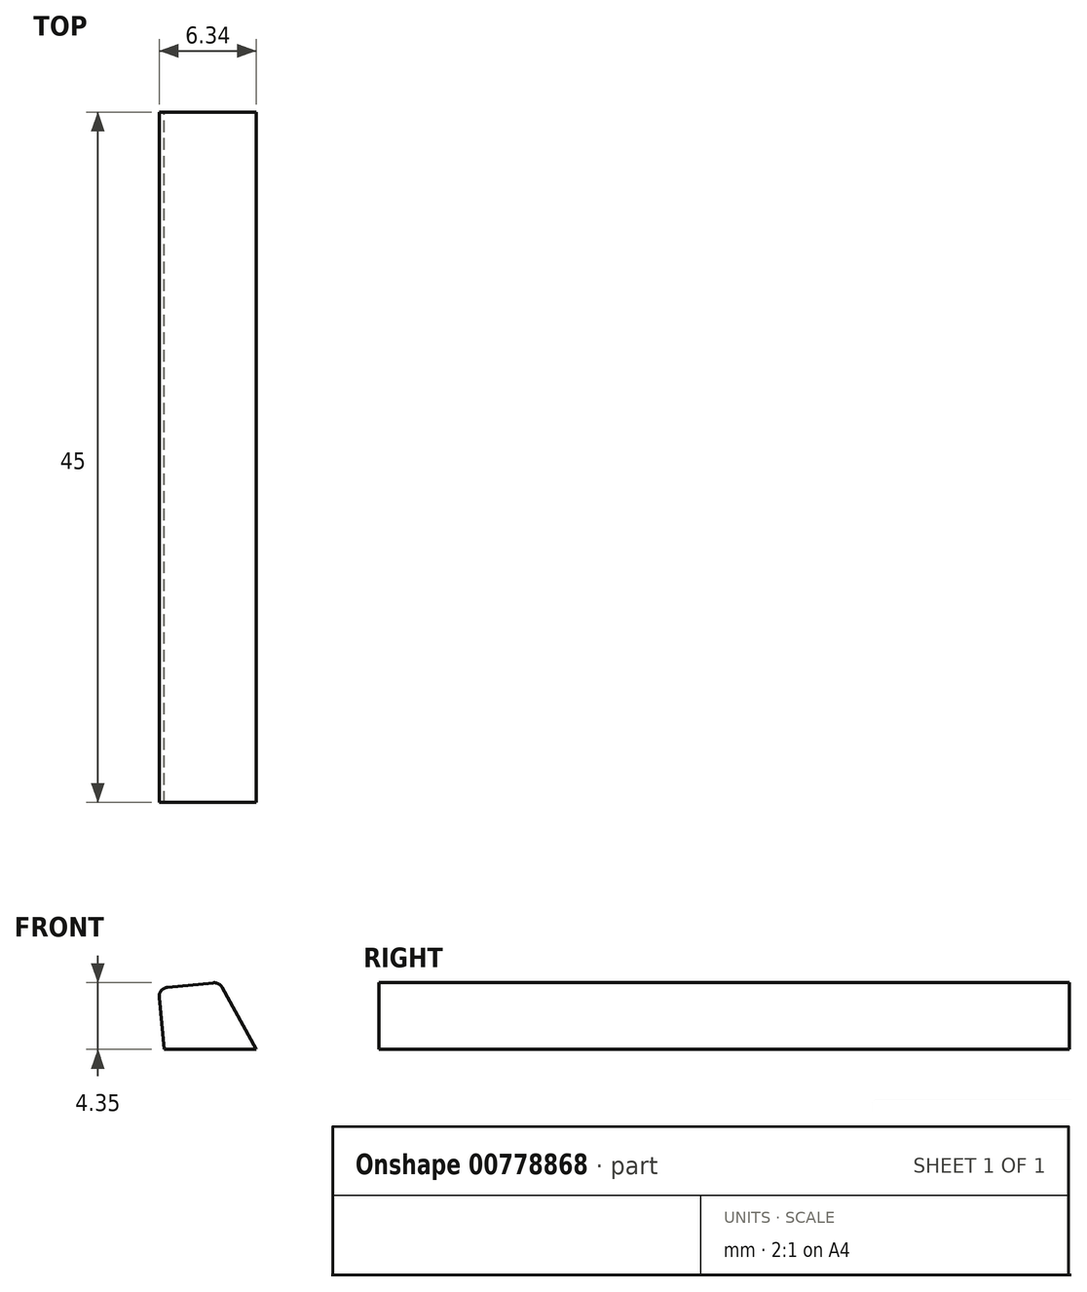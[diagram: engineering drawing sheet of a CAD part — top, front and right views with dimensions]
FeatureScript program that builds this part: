
annotation { "Feature Type Name" : "Feature", "Feature Type Description" : "" }
export const myFeature = defineFeature(function(context is Context, id is Id, definition is map)
    precondition{}
    {
        {
            var Q0;
            Q0=qCreatedBy(makeId("Front.planeOp"),FACE);
            var sketch = newSketch(context, id + "F0", { "sketchPlane" : qUnion([Q0])});
            skLineSegment(sketch, "E0", {"start": v(1.24, 0) * mm, "end": v(2.43, 0.12) * mm});
            skLineSegment(sketch, "E1", {"start": v(2.43, 0.12) * mm, "end": v(2.03, 4.1) * mm});
            skLineSegment(sketch, "E2", {"start": v(2.03, 4.1) * mm, "end": v(6.01, 4.5) * mm});
            skLineSegment(sketch, "E3", {"start": v(8.43, 0.13) * mm, "end": v(6.01, 4.5) * mm});
            skLineSegment(sketch, "E4", {"start": v(8.43, 0.13) * mm, "end": v(9.4, 0.41) * mm});
            skLineSegment(sketch, "E5", {"start": v(9.4, 0.41) * mm, "end": v(7.31, 3.24) * mm});
            skFitSpline(sketch, "E6", {"points": [v(1.24, 0) * mm, v(7.31, 3.24) * mm], "startDerivative": vector(-3.72, 16.94) * mm, "endDerivative": vector(6.9, -10.03) * mm});
            skPoint(sketch, "E7", {"position": v(4.69, 6.14) * mm});
            skLineSegment(sketch, "E8", {"start": v(2.43, 0.12) * mm, "end": v(8.43, 0.13) * mm});
            skSolve(sketch);
        }
        {
            var Q0;
            Q0=makeQuery(id+"F0.imprint","IMPRINT",FACE,{"disambiguationData":[TD([[makeQuery(id+"F0.imprint","IMPRINT",EDGE,{"derivedFrom":sQuery(id+"F0.wireOp",EDGE,"E1")}),-1.0]])]});
            extrude(context, id + "F1", {"entities" : qUnion([Q0]), "depth" : 45 * mm, "offsetDistance" : 25 * mm});
        }
        {
            var Q0;
            Q0=makeQuery(id+"F1.opExtrude","SWEPT_EDGE",EDGE,{"disambiguationData":[OSD([sQuery(id+"F0.wireOp",EDGE,"E1"),sQuery(id+"F0.wireOp",EDGE,"E2")])]});
            var Q1;
            Q1=makeQuery(id+"F1.opExtrude","SWEPT_EDGE",EDGE,{"disambiguationData":[OSD([sQuery(id+"F0.wireOp",EDGE,"E2"),sQuery(id+"F0.wireOp",EDGE,"E3")])]});
            fillet(context, id + "F2", {"entities" : qUnion([Q0, Q1]), "tangentPropagation" : true, "radius" : 0.6 * mm, "defaultsChanged" : false, "vertexSettings" : [], "allowEdgeOverflow" : false});
        }
    });
